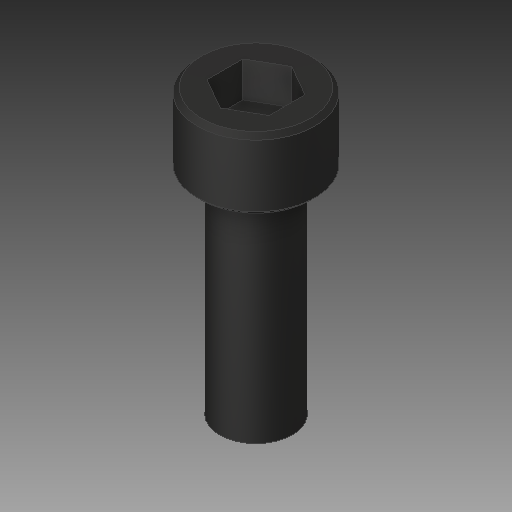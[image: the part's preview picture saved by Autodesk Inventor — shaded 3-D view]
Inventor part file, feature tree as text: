
AUTODESK INVENTOR PART (.ipt)
format: ipt  version: 2018 (Build 220112000, 112)  size: 103,936 bytes
history: native  units: in
note: dims shown in document units (in); Inventor stores cm internally (conversion verified against a paired STEP export)
features: chamfer x1
ambient origin geometry x8: Origin, YZ Plane, XZ Plane, XY Plane, X Axis, Y Axis, Z Axis, Center Point
bodies: Solid1 (feature_tree)
feature tree (1):
  chamfer  "Chamfer2"  [1 undecoded]
note: 1 required parameter value undecoded (feature->parameter linkage not recoverable at this tier; creation-order binding heuristic only, values carry confidence <= 0.55)
